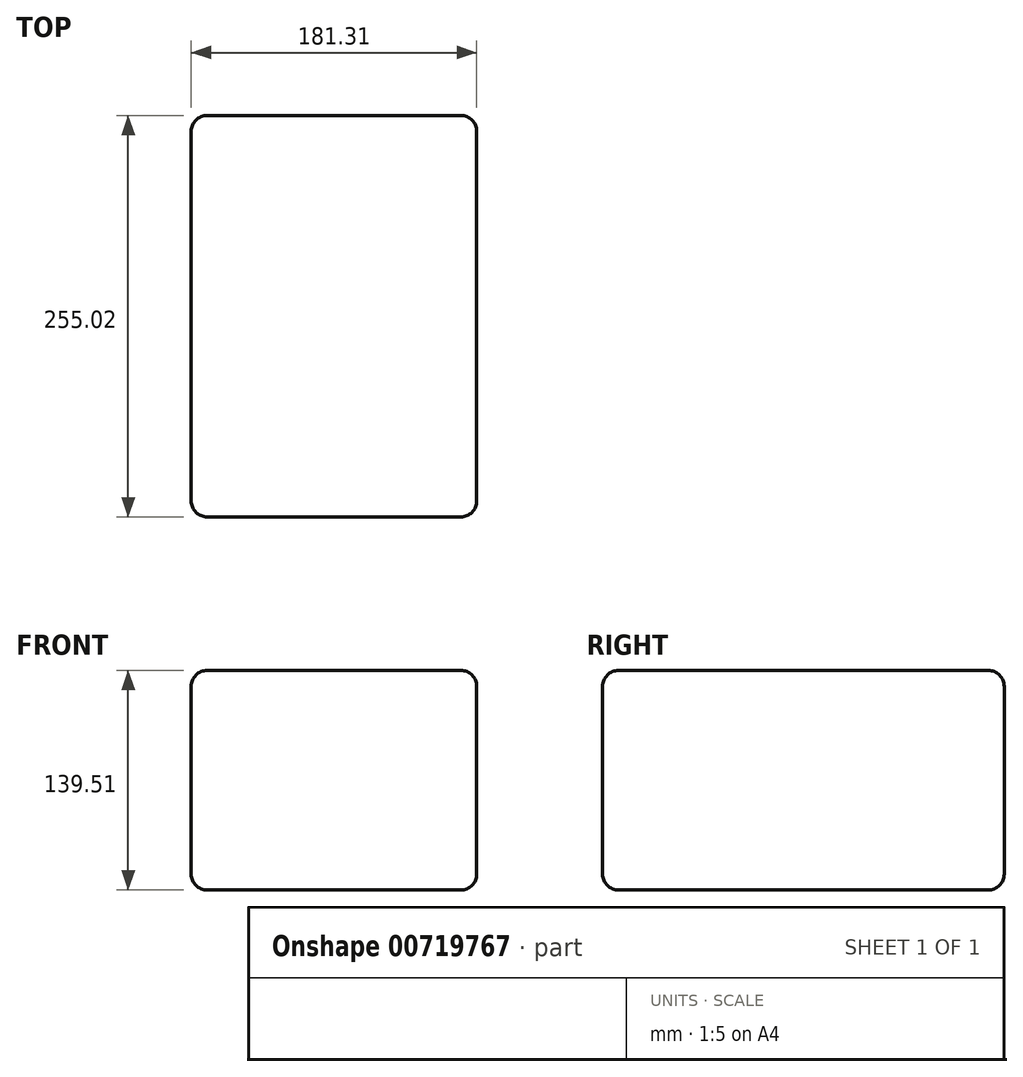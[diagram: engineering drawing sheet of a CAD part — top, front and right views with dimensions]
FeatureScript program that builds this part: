
annotation { "Feature Type Name" : "Feature", "Feature Type Description" : "" }
export const myFeature = defineFeature(function(context is Context, id is Id, definition is map)
    precondition{}
    {
        {
            var Q0;
            Q0=qCreatedBy(makeId("Front.planeOp"),FACE);
            var sketch = newSketch(context, id + "F0", { "sketchPlane" : qUnion([Q0])});
            skLineSegment(sketch, "E0.bottom", {"start": v(13.18, 50.27) * mm, "end": v(194.5, 50.27) * mm});
            skLineSegment(sketch, "E0.top", {"start": v(13.18, -89.24) * mm, "end": v(194.5, -89.24) * mm});
            skLineSegment(sketch, "E0.left", {"start": v(13.18, 50.27) * mm, "end": v(13.18, -89.24) * mm});
            skLineSegment(sketch, "E0.right", {"start": v(194.5, 50.27) * mm, "end": v(194.5, -89.24) * mm});
            skSolve(sketch);
        }
        {
            var Q0;
            Q0=makeQuery(id+"F0.imprint","IMPRINT",FACE,{"disambiguationData":[TD([[makeQuery(id+"F0.imprint","IMPRINT",EDGE,{"derivedFrom":sQuery(id+"F0.wireOp",EDGE,"E0.bottom")}),-1.0]])]});
            extrude(context, id + "F1", {"entities" : qUnion([Q0]), "oppositeDirection" : true, "depth" : 255.02 * mm, "offsetDistance" : 25.4 * mm});
        }
        {
            var Q0;
            Q0=makeQuery(id+"F1.opExtrude","SWEPT_EDGE",EDGE,{"disambiguationData":[OSD([sQuery(id+"F0.wireOp",EDGE,"E0.bottom"),sQuery(id+"F0.wireOp",EDGE,"E0.right")])]});
            fillet(context, id + "F2", {"entities" : qUnion([Q0]), "radius" : 10.16 * mm, "tangentPropagation" : true, "allowEdgeOverflow" : false});
        }
        {
            var Q0;
            Q0=makeQuery(id+"F1.opExtrude","SWEPT_EDGE",EDGE,{"disambiguationData":[OSD([sQuery(id+"F0.wireOp",EDGE,"E0.bottom"),sQuery(id+"F0.wireOp",EDGE,"E0.left")])]});
            var Q1;
            Q1=makeQuery(id+"F1.opExtrude","SWEPT_EDGE",EDGE,{"disambiguationData":[OSD([sQuery(id+"F0.wireOp",EDGE,"E0.top"),sQuery(id+"F0.wireOp",EDGE,"E0.left")])]});
            var Q2;
            Q2=makeQuery(id+"F1.opExtrude","CAP_EDGE",EDGE,{"disambiguationData":[OSD([sQuery(id+"F0.wireOp",EDGE,"E0.bottom")])],"isStart":false});
            var Q3;
            Q3=makeQuery(id+"F1.opExtrude","CAP_EDGE",EDGE,{"disambiguationData":[OSD([sQuery(id+"F0.wireOp",EDGE,"E0.top")])],"isStart":false});
            var Q4;
            Q4=makeQuery(id+"F1.opExtrude","CAP_EDGE",EDGE,{"disambiguationData":[OSD([sQuery(id+"F0.wireOp",EDGE,"E0.left")])],"isStart":false});
            var Q5;
            Q5=makeQuery(id+"F1.opExtrude","CAP_EDGE",EDGE,{"disambiguationData":[OSD([sQuery(id+"F0.wireOp",EDGE,"E0.right")])],"isStart":false});
            var Q6;
            Q6=makeQuery(id+"F1.opExtrude","CAP_EDGE",EDGE,{"disambiguationData":[OSD([sQuery(id+"F0.wireOp",EDGE,"E0.left")])],"isStart":true});
            var Q7;
            Q7=makeQuery(id+"F1.opExtrude","CAP_EDGE",EDGE,{"disambiguationData":[OSD([sQuery(id+"F0.wireOp",EDGE,"E0.top")])],"isStart":true});
            var Q8;
            Q8=makeQuery(id+"F1.opExtrude","CAP_EDGE",EDGE,{"disambiguationData":[OSD([sQuery(id+"F0.wireOp",EDGE,"E0.right")])],"isStart":true});
            var Q9;
            Q9=makeQuery(id+"F1.opExtrude","CAP_EDGE",EDGE,{"disambiguationData":[OSD([sQuery(id+"F0.wireOp",EDGE,"E0.bottom")])],"isStart":true});
            var Q10;
            Q10=makeQuery(id+"F1.opExtrude","SWEPT_EDGE",EDGE,{"disambiguationData":[OSD([sQuery(id+"F0.wireOp",EDGE,"E0.top"),sQuery(id+"F0.wireOp",EDGE,"E0.right")])]});
            fillet(context, id + "F3", {"entities" : qUnion([Q0, Q1, Q2, Q3, Q4, Q5, Q6, Q7, Q8, Q9, Q10]), "radius" : 10.16 * mm, "tangentPropagation" : true, "allowEdgeOverflow" : false});
        }
    });
